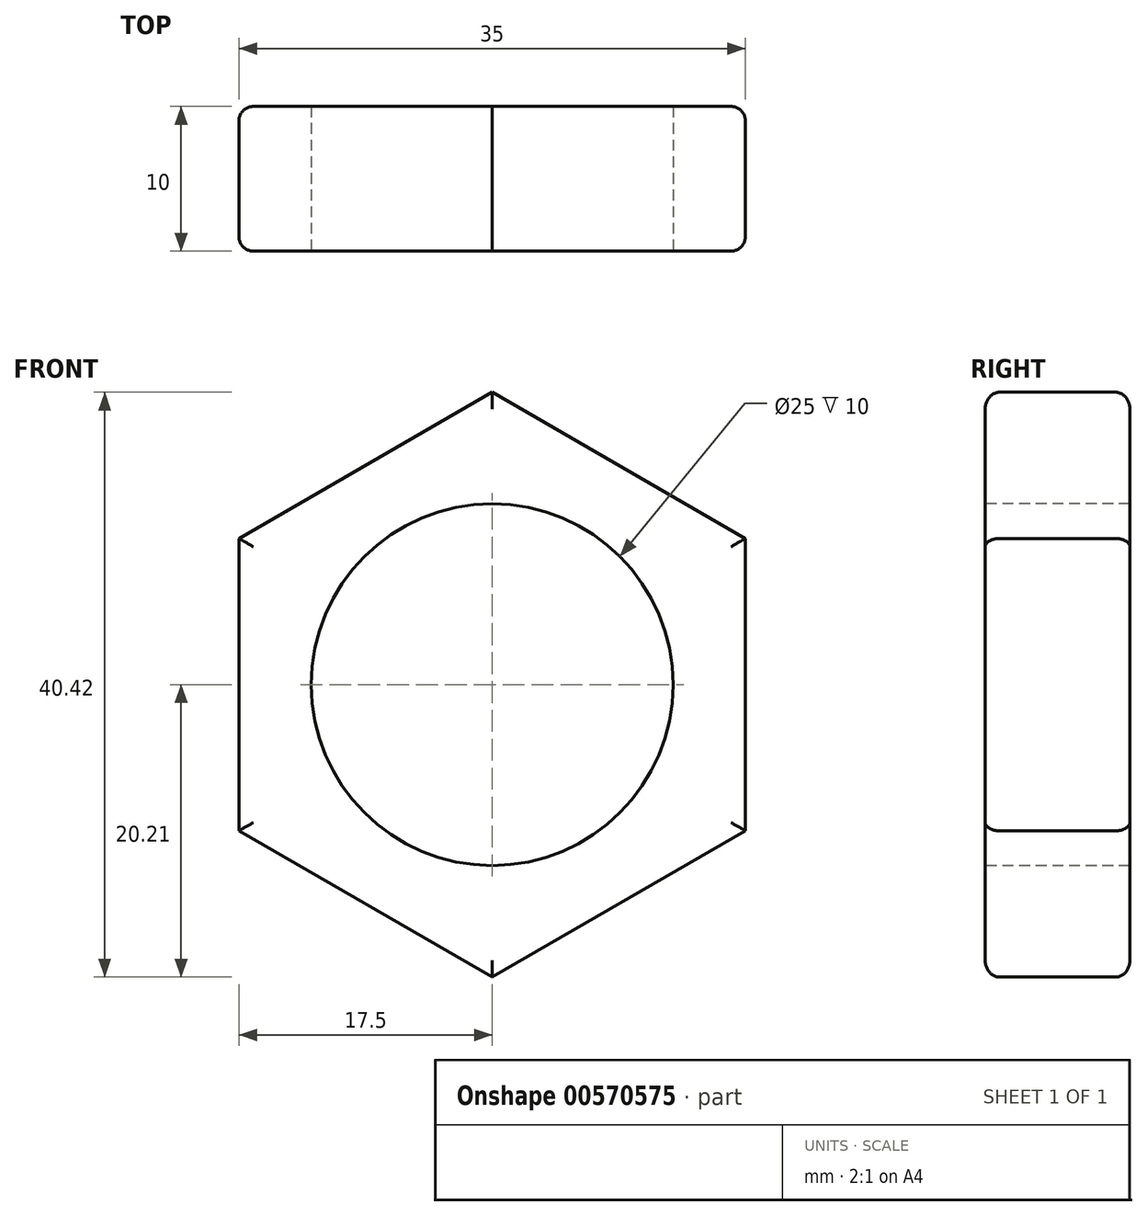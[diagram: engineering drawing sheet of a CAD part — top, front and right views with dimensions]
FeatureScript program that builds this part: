
annotation { "Feature Type Name" : "Feature", "Feature Type Description" : "" }
export const myFeature = defineFeature(function(context is Context, id is Id, definition is map)
    precondition{}
    {
        {
            var Q0;
            Q0=qCreatedBy(makeId("Front.planeOp"),FACE);
            var sketch = newSketch(context, id + "F0", { "sketchPlane" : qUnion([Q0])});
            skCircle(sketch, "E0.cCircle", {"center": v(0, 0) * mm, "radius": 17.5 * mm, "construction": true});
            skLineSegment(sketch, "E0.0", {"start": v(0, 20.2) * mm, "end": v(17.5, 10.1) * mm});
            skLineSegment(sketch, "E0.1", {"start": v(17.5, 10.1) * mm, "end": v(17.5, -10.1) * mm});
            skLineSegment(sketch, "E0.2", {"start": v(17.5, -10.1) * mm, "end": v(0, -20.2) * mm});
            skLineSegment(sketch, "E0.3", {"start": v(0, -20.2) * mm, "end": v(-17.5, -10.1) * mm});
            skLineSegment(sketch, "E0.4", {"start": v(-17.5, -10.1) * mm, "end": v(-17.5, 10.1) * mm});
            skLineSegment(sketch, "E0.5", {"start": v(-17.5, 10.1) * mm, "end": v(0, 20.2) * mm});
            skPoint(sketch, "E0.0.midPoint", {"position": v(8.75, 15.16) * mm});
            skSolve(sketch);
        }
        {
            var Q0;
            Q0 = qSketchRegion(id + "F0", true);
            extrude(context, id + "F1", {"entities" : qUnion([Q0]), "depth" : 10 * mm, "offsetDistance" : 25 * mm});
        }
        {
            var Q0;
            Q0=makeQuery(id+"F1.opExtrude","CAP_FACE",FACE,{"disambiguationData":[OSD([sQuery(id+"F0.wireOp",EDGE,"E0.0"),sQuery(id+"F0.wireOp",EDGE,"E0.1"),sQuery(id+"F0.wireOp",EDGE,"E0.2"),sQuery(id+"F0.wireOp",EDGE,"E0.3"),sQuery(id+"F0.wireOp",EDGE,"E0.4"),sQuery(id+"F0.wireOp",EDGE,"E0.5")])],"isStart":false});
            var sketch = newSketch(context, id + "F2", { "sketchPlane" : qUnion([Q0])});
            skCircle(sketch, "E1", {"center": v(0, 0) * mm, "radius": 12.5 * mm});
            skSolve(sketch);
        }
        {
            var Q0;
            Q0 = qSketchRegion(id + "F2", true);
            extrude(context, id + "F3", {"entities" : qUnion([Q0]), "operationType" : NewBodyOperationType.REMOVE, "endBound" : BoundingType.THROUGH_ALL, "oppositeDirection" : true, "depth" : 25 * mm, "offsetDistance" : 25 * mm});
        }
        {
            var Q0;
            Q0=makeQuery(id+"F1.opExtrude","CAP_EDGE",EDGE,{"disambiguationData":[OSD([sQuery(id+"F0.wireOp",EDGE,"E0.0")])],"isStart":false});
            var Q1;
            Q1=makeQuery(id+"F1.opExtrude","CAP_EDGE",EDGE,{"disambiguationData":[OSD([sQuery(id+"F0.wireOp",EDGE,"E0.5")])],"isStart":false});
            var Q2;
            Q2=makeQuery(id+"F1.opExtrude","CAP_EDGE",EDGE,{"disambiguationData":[OSD([sQuery(id+"F0.wireOp",EDGE,"E0.1")])],"isStart":false});
            var Q3;
            Q3=makeQuery(id+"F1.opExtrude","CAP_EDGE",EDGE,{"disambiguationData":[OSD([sQuery(id+"F0.wireOp",EDGE,"E0.2")])],"isStart":false});
            var Q4;
            Q4=makeQuery(id+"F1.opExtrude","CAP_EDGE",EDGE,{"disambiguationData":[OSD([sQuery(id+"F0.wireOp",EDGE,"E0.3")])],"isStart":false});
            var Q5;
            Q5=makeQuery(id+"F1.opExtrude","CAP_EDGE",EDGE,{"disambiguationData":[OSD([sQuery(id+"F0.wireOp",EDGE,"E0.4")])],"isStart":false});
            var Q6;
            Q6=makeQuery(id+"F1.opExtrude","CAP_EDGE",EDGE,{"disambiguationData":[OSD([sQuery(id+"F0.wireOp",EDGE,"E0.0")])],"isStart":true});
            var Q7;
            Q7=makeQuery(id+"F1.opExtrude","CAP_EDGE",EDGE,{"disambiguationData":[OSD([sQuery(id+"F0.wireOp",EDGE,"E0.5")])],"isStart":true});
            var Q8;
            Q8=makeQuery(id+"F1.opExtrude","CAP_EDGE",EDGE,{"disambiguationData":[OSD([sQuery(id+"F0.wireOp",EDGE,"E0.4")])],"isStart":true});
            var Q9;
            Q9=makeQuery(id+"F1.opExtrude","CAP_EDGE",EDGE,{"disambiguationData":[OSD([sQuery(id+"F0.wireOp",EDGE,"E0.3")])],"isStart":true});
            var Q10;
            Q10=makeQuery(id+"F1.opExtrude","CAP_EDGE",EDGE,{"disambiguationData":[OSD([sQuery(id+"F0.wireOp",EDGE,"E0.2")])],"isStart":true});
            var Q11;
            Q11=makeQuery(id+"F1.opExtrude","CAP_EDGE",EDGE,{"disambiguationData":[OSD([sQuery(id+"F0.wireOp",EDGE,"E0.1")])],"isStart":true});
            fillet(context, id + "F4", {"entities" : qUnion([Q0, Q1, Q2, Q3, Q4, Q5, Q6, Q7, Q8, Q9, Q10, Q11]), "radius" : 1 * mm, "tangentPropagation" : true, "allowEdgeOverflow" : false});
        }
    });
